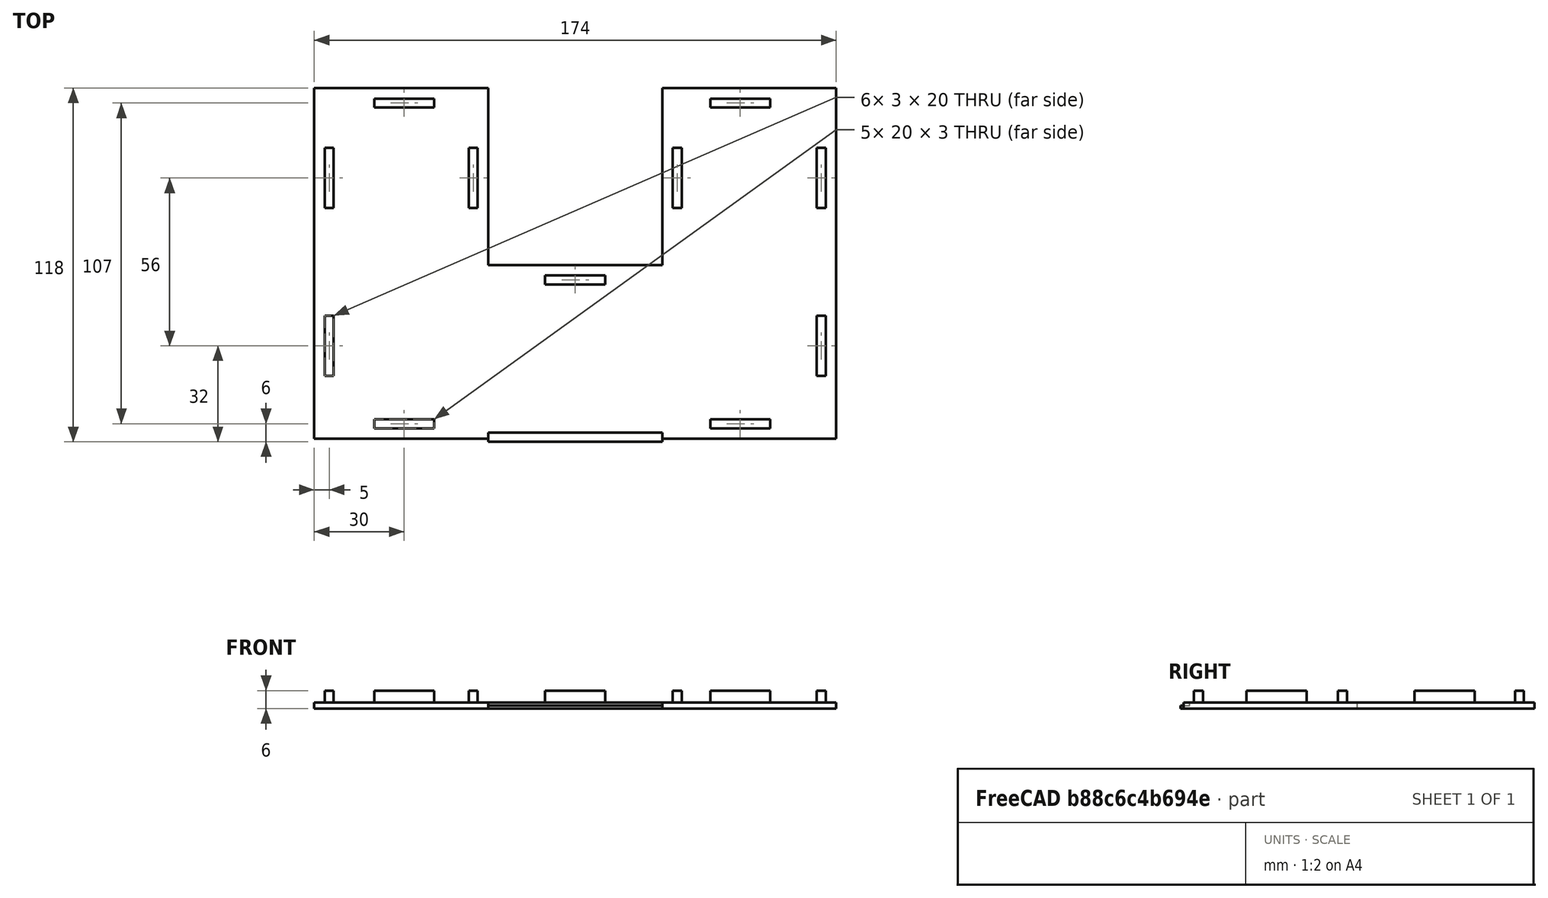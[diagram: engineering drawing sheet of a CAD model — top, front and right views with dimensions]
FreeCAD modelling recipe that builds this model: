
FCSTD DOCUMENT  (FreeCAD 0.21R33694 (Git))
Label: maze_cover_C
License: All rights reserved
LicenseURL: https://en.wikipedia.org/wiki/All_rights_reserved
objects: Part::Box×15, Part::MultiFuse×1
note: 16 computed .brp shape members not serialized (recipe doc carries the construction recipe); baked Part::Feature solids carry a one-line shape summary decoded from their .brp

FEATURE [Part::Box] Box  label="Cube"
  AttacherType = Attacher::AttachEngine3D
  Height = 2
  Length = 58
  Placement = pos=(58,2,0) rot=(0,0,1;0rad)
  Width = 56
FEATURE [Part::Box] Box001  label="Cube001"
  AttacherType = Attacher::AttachEngine3D
  Height = 2
  Length = 58
  Width = 117
FEATURE [Part::Box] Box002  label="Cube002"
  AttacherType = Attacher::AttachEngine3D
  Height = 2
  Length = 58
  Placement = pos=(116,0,0) rot=(0,0,1;0rad)
  Width = 117
FEATURE [Part::Box] Box003  label="Cube003"
  AttacherType = Attacher::AttachEngine3D
  Height = 6
  Length = 20
  Placement = pos=(20,110.5,0) rot=(0,0,1;0rad)
  Width = 3
FEATURE [Part::Box] Box004  label="Cube004"
  AttacherType = Attacher::AttachEngine3D
  Height = 6
  Length = 20
  Placement = pos=(20,3.5,0) rot=(0,0,1;0rad)
  Width = 3
FEATURE [Part::Box] Box005  label="Cube005"
  AttacherType = Attacher::AttachEngine3D
  Height = 6
  Length = 20
  Placement = pos=(132,3.5,0) rot=(0,0,1;0rad)
  Width = 3
FEATURE [Part::Box] Box006  label="Cube006"
  AttacherType = Attacher::AttachEngine3D
  Height = 6
  Length = 20
  Placement = pos=(132,110.5,0) rot=(0,0,1;0rad)
  Width = 3
FEATURE [Part::Box] Box007  label="Cube007"
  AttacherType = Attacher::AttachEngine3D
  Height = 6
  Length = 20
  Placement = pos=(119.5,97,0) rot=(0,0,-1;1.5708rad)
  Width = 3
FEATURE [Part::Box] Box008  label="Cube008"
  AttacherType = Attacher::AttachEngine3D
  Height = 6
  Length = 20
  Placement = pos=(167.5,41,0) rot=(0,0,-1;1.5708rad)
  Width = 3
FEATURE [Part::Box] Box009  label="Cube009"
  AttacherType = Attacher::AttachEngine3D
  Height = 6
  Length = 20
  Placement = pos=(167.5,97,0) rot=(0,0,-1;1.5708rad)
  Width = 3
FEATURE [Part::Box] Box010  label="Cube010"
  AttacherType = Attacher::AttachEngine3D
  Height = 6
  Length = 20
  Placement = pos=(51.5,97,0) rot=(0,0,-1;1.5708rad)
  Width = 3
FEATURE [Part::Box] Box011  label="Cube011"
  AttacherType = Attacher::AttachEngine3D
  Height = 6
  Length = 20
  Placement = pos=(3.5,97,0) rot=(0,0,-1;1.5708rad)
  Width = 3
  expr: .Placement.Base.x = 3.5 mm
FEATURE [Part::Box] Box012  label="Cube012"
  AttacherType = Attacher::AttachEngine3D
  Height = 6
  Length = 20
  Placement = pos=(3.5,41,0) rot=(0,0,-1;1.5708rad)
  Width = 3
FEATURE [Part::Box] Box013  label="Cube013"
  AttacherType = Attacher::AttachEngine3D
  Height = 6
  Length = 20
  Placement = pos=(77,51.5,0) rot=(0,0,1;0rad)
  Width = 3
FEATURE [Part::Box] Box014  label="Cube014"
  AttacherType = Attacher::AttachEngine3D
  Height = 1
  Length = 58
  Placement = pos=(58,-1,0) rot=(0,0,1;0rad)
  Width = 3
FEATURE [Part::MultiFuse] Fusion
  Shapes = -> [Box014,Box013,Box012,Box011,Box010,Box009,Box008,Box007,Box006,Box005,Box004,Box003,Box002,Box001,Box]
